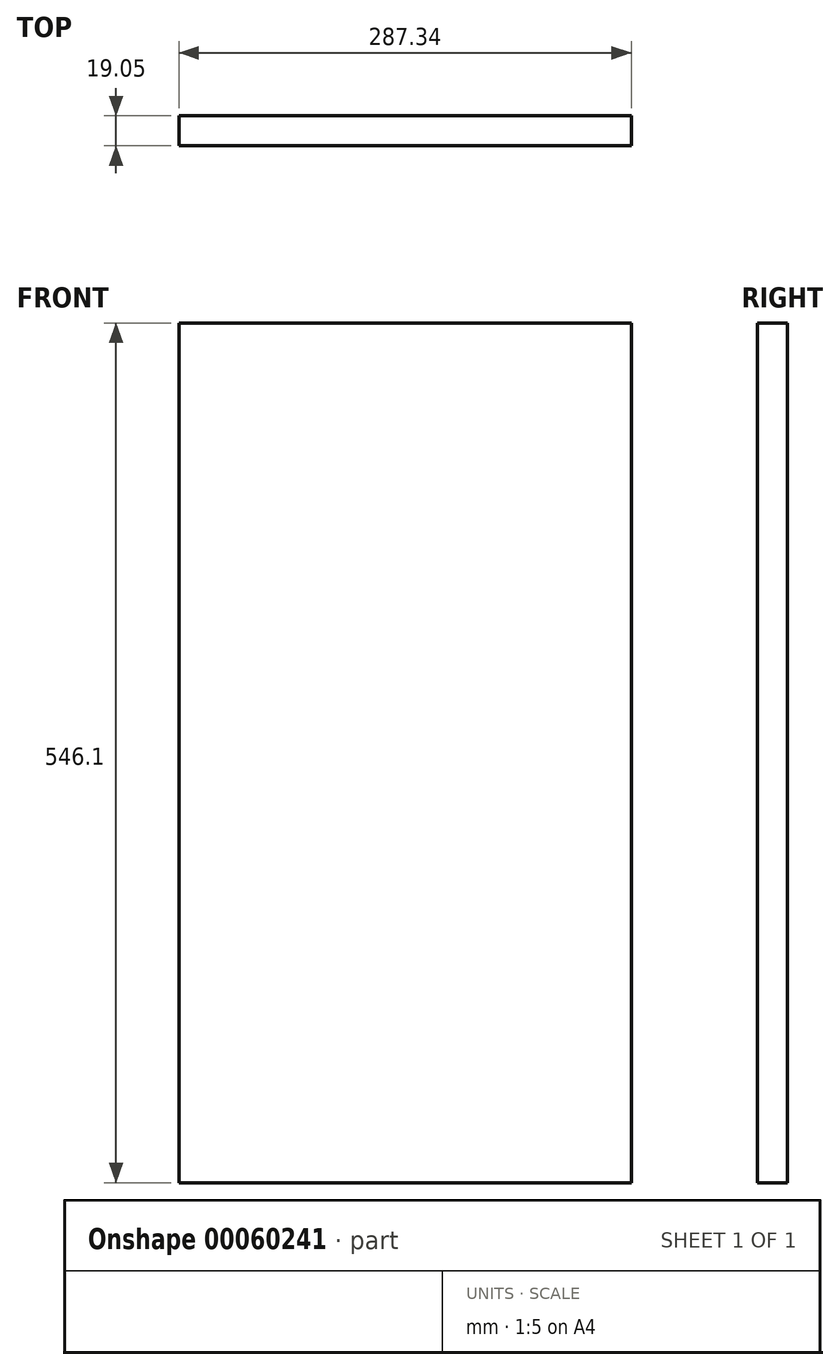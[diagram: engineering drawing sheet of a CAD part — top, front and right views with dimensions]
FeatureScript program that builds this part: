
annotation { "Feature Type Name" : "Feature", "Feature Type Description" : "" }
export const myFeature = defineFeature(function(context is Context, id is Id, definition is map)
    precondition{}
    {
        {
            var Q0;
            Q0=qCreatedBy(makeId("Front.planeOp"),FACE);
            var sketch = newSketch(context, id + "F0", { "sketchPlane" : qUnion([Q0])});
            skLineSegment(sketch, "E0.bottom", {"start": v(0, 0) * mm, "end": v(287.34, 0) * mm});
            skLineSegment(sketch, "E0.top", {"start": v(0, 546.1) * mm, "end": v(287.34, 546.1) * mm});
            skLineSegment(sketch, "E0.left", {"start": v(0, 0) * mm, "end": v(0, 546.1) * mm});
            skLineSegment(sketch, "E0.right", {"start": v(287.34, 0) * mm, "end": v(287.34, 546.1) * mm});
            skSolve(sketch);
        }
        {
            var Q0;
            Q0=makeQuery(id+"F0.imprint","IMPRINT",FACE,{"disambiguationData":[TD([[makeQuery(id+"F0.imprint","IMPRINT",EDGE,{"derivedFrom":sQuery(id+"F0.wireOp",EDGE,"E0.bottom")}),1.0]])]});
            extrude(context, id + "F1", {"entities" : qUnion([Q0]), "depth" : 19.05 * mm});
        }
    });
